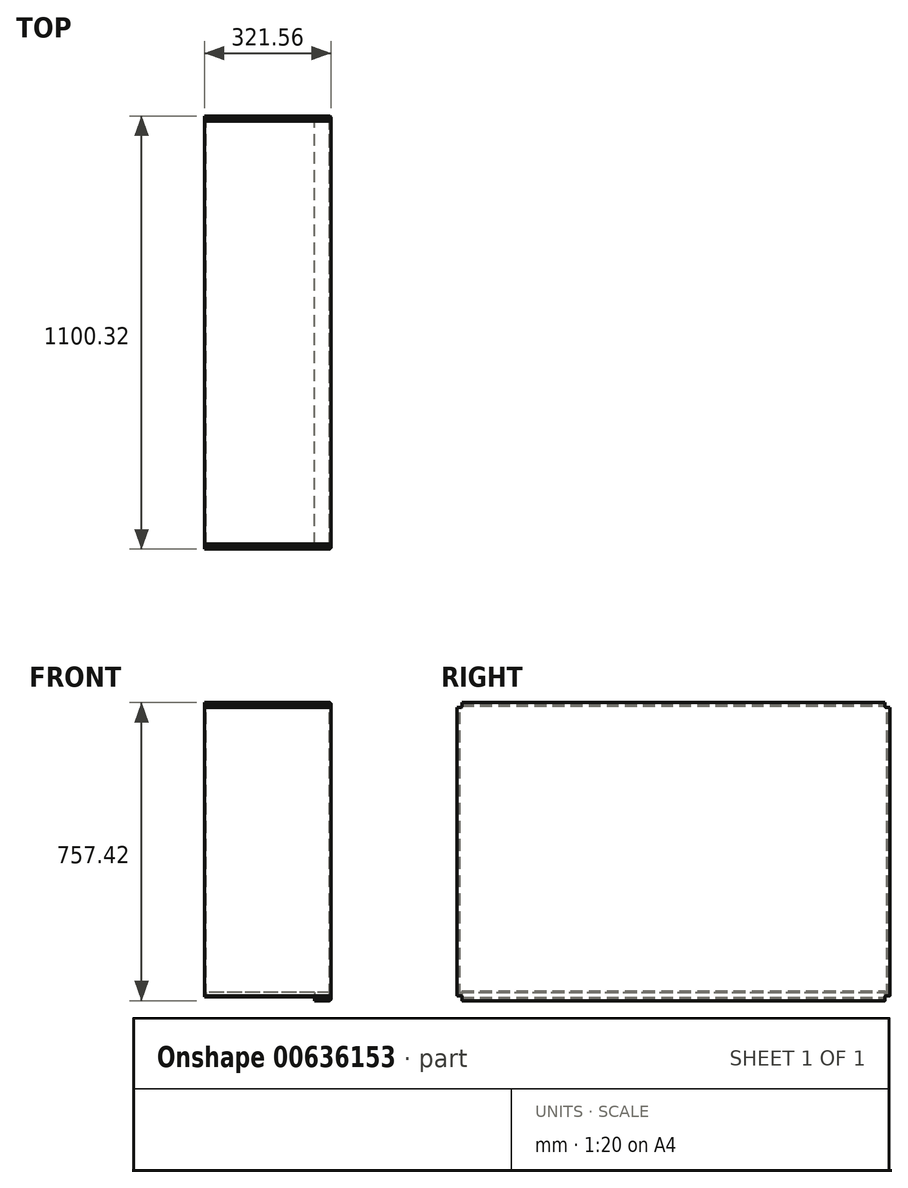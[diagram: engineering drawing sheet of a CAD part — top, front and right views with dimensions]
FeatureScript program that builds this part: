
annotation { "Feature Type Name" : "Feature", "Feature Type Description" : "" }
export const myFeature = defineFeature(function(context is Context, id is Id, definition is map)
    precondition{}
    {
        {
            var Q0;
            Q0=qCreatedBy(makeId("Right.planeOp"),FACE);
            var sketch = newSketch(context, id + "F0", { "sketchPlane" : qUnion([Q0])});
            skLineSegment(sketch, "E0.bottom", {"start": v(0, 0) * mm, "end": v(1092.2, 0) * mm});
            skLineSegment(sketch, "E0.top", {"start": v(0, 749.3) * mm, "end": v(1092.2, 749.3) * mm});
            skLineSegment(sketch, "E0.left", {"start": v(0, 0) * mm, "end": v(0, 749.3) * mm});
            skLineSegment(sketch, "E0.right", {"start": v(1092.2, 0) * mm, "end": v(1092.2, 749.3) * mm});
            skSolve(sketch);
        }
        {
            var Q0;
            Q0 = qSketchRegion(id + "F0", true);
            extrude(context, id + "F1", {"entities" : qUnion([Q0]), "depth" : 317.5 * mm, "offsetDistance" : 25.4 * mm});
        }
        {
            var Q0;
            Q0=makeQuery(id+"F1.opExtrude","CAP_FACE",FACE,{"disambiguationData":[OSD([sQuery(id+"F0.wireOp",EDGE,"E0.bottom"),sQuery(id+"F0.wireOp",EDGE,"E0.top"),sQuery(id+"F0.wireOp",EDGE,"E0.left"),sQuery(id+"F0.wireOp",EDGE,"E0.right")])],"isStart":false});
            shell(context, id + "F2", {"entities" : qUnion([Q0]), "thickness" : 4.06 * mm});
        }
        {
            var Q0;
            Q0=makeQuery(id+"F1.opExtrude","SWEPT_FACE",FACE,{"disambiguationData":[OSD([sQuery(id+"F0.wireOp",EDGE,"E0.bottom")])]});
            var sketch = newSketch(context, id + "F3", { "sketchPlane" : qUnion([Q0])});
            skLineSegment(sketch, "E1.bottom", {"start": v(317.5, 0) * mm, "end": v(38.1, 0) * mm});
            skLineSegment(sketch, "E1.top", {"start": v(317.5, -1717.8) * mm, "end": v(38.1, -1717.8) * mm});
            skLineSegment(sketch, "E1.left", {"start": v(317.5, 0) * mm, "end": v(317.5, -1717.8) * mm});
            skLineSegment(sketch, "E1.right", {"start": v(38.1, 0) * mm, "end": v(38.1, -1717.8) * mm});
            skSolve(sketch);
        }
        {
            var Q0;
            Q0 = qSketchRegion(id + "F3", true);
            extrude(context, id + "F4", {"entities" : qUnion([Q0]), "operationType" : NewBodyOperationType.REMOVE, "oppositeDirection" : true, "depth" : 4.06 * mm, "offsetDistance" : 25.4 * mm});
        }
        {
            var Q0;
            Q0=makeQuery(id+"F1.opExtrude","CAP_FACE",FACE,{"disambiguationData":[OSD([sQuery(id+"F0.wireOp",EDGE,"E0.bottom"),sQuery(id+"F0.wireOp",EDGE,"E0.top"),sQuery(id+"F0.wireOp",EDGE,"E0.left"),sQuery(id+"F0.wireOp",EDGE,"E0.right")])],"isStart":true});
            var sketch = newSketch(context, id + "F5", { "sketchPlane" : qUnion([Q0])});
            skLineSegment(sketch, "E2.bottom", {"start": v(-1092.2, 0) * mm, "end": v(-1085.85, 0) * mm});
            skLineSegment(sketch, "E2.top", {"start": v(-1092.2, 6.35) * mm, "end": v(-1088.39, 6.35) * mm});
            skLineSegment(sketch, "E2.left", {"start": v(-1092.2, 0) * mm, "end": v(-1092.2, 6.35) * mm});
            skLineSegment(sketch, "E2.right", {"start": v(-1085.85, 0) * mm, "end": v(-1085.85, 3.81) * mm});
            skLineSegment(sketch, "E3.bottom", {"start": v(-1092.2, 749.3) * mm, "end": v(-1085.85, 749.3) * mm});
            skLineSegment(sketch, "E3.top", {"start": v(-1092.2, 742.95) * mm, "end": v(-1088.4, 742.95) * mm});
            skLineSegment(sketch, "E3.left", {"start": v(-1092.2, 749.3) * mm, "end": v(-1092.2, 742.95) * mm});
            skLineSegment(sketch, "E3.right", {"start": v(-1085.85, 749.3) * mm, "end": v(-1085.85, 745.5) * mm});
            skLineSegment(sketch, "E4.bottom", {"start": v(0, 749.3) * mm, "end": v(-6.35, 749.3) * mm});
            skLineSegment(sketch, "E4.top", {"start": v(0, 742.95) * mm, "end": v(-3.8, 742.95) * mm});
            skLineSegment(sketch, "E4.left", {"start": v(0, 749.3) * mm, "end": v(0, 742.95) * mm});
            skLineSegment(sketch, "E4.right", {"start": v(-6.35, 749.3) * mm, "end": v(-6.35, 745.5) * mm});
            skLineSegment(sketch, "E5.bottom", {"start": v(0, 0) * mm, "end": v(-6.35, 0) * mm});
            skLineSegment(sketch, "E5.top", {"start": v(0, 6.35) * mm, "end": v(-3.8, 6.35) * mm});
            skLineSegment(sketch, "E5.left", {"start": v(0, 0) * mm, "end": v(0, 6.35) * mm});
            skLineSegment(sketch, "E5.right", {"start": v(-6.35, 0) * mm, "end": v(-6.35, 3.81) * mm});
            skPoint(sketch, "E6.visualSharp", {"position": v(-1085.85, 742.95) * mm});
            skArc(sketch, "E6.filletArc", {"start": v(-1088.4, 742.95) * mm, "mid": v(-1086.6, 743.7) * mm, "end": v(-1085.85, 745.5) * mm});
            skPoint(sketch, "E7.visualSharp", {"position": v(-6.35, 742.95) * mm});
            skArc(sketch, "E7.filletArc", {"start": v(-6.35, 745.5) * mm, "mid": v(-5.6, 743.7) * mm, "end": v(-3.8, 742.95) * mm});
            skPoint(sketch, "E8.visualSharp", {"position": v(-6.35, 6.35) * mm});
            skArc(sketch, "E8.filletArc", {"start": v(-3.8, 6.35) * mm, "mid": v(-5.6, 5.6) * mm, "end": v(-6.35, 3.81) * mm});
            skPoint(sketch, "E9.visualSharp", {"position": v(-1085.85, 6.35) * mm});
            skArc(sketch, "E9.filletArc", {"start": v(-1085.85, 3.81) * mm, "mid": v(-1086.6, 5.6) * mm, "end": v(-1088.39, 6.35) * mm});
            skSolve(sketch);
        }
        {
            var Q0;
            Q0 = qSketchRegion(id + "F5", true);
            extrude(context, id + "F6", {"entities" : qUnion([Q0]), "operationType" : NewBodyOperationType.REMOVE, "endBound" : BoundingType.THROUGH_ALL, "oppositeDirection" : true, "depth" : 25.4 * mm, "offsetDistance" : 25.4 * mm});
        }
        {
            var Q0;
            Q0=makeQuery(id+"F1.opExtrude","CAP_EDGE",EDGE,{"disambiguationData":[OSD([sQuery(id+"F0.wireOp",EDGE,"E0.right")])],"isStart":true});
            var Q1;
            Q1=makeQuery(id+"F1.opExtrude","CAP_EDGE",EDGE,{"disambiguationData":[OSD([sQuery(id+"F0.wireOp",EDGE,"E0.bottom")])],"isStart":true});
            var Q2;
            Q2=makeQuery(id+"F1.opExtrude","CAP_EDGE",EDGE,{"disambiguationData":[OSD([sQuery(id+"F0.wireOp",EDGE,"E0.left")])],"isStart":true});
            var Q3;
            Q3=makeQuery(id+"F1.opExtrude","CAP_EDGE",EDGE,{"disambiguationData":[OSD([sQuery(id+"F0.wireOp",EDGE,"E0.top")])],"isStart":true});
            fillet(context, id + "F7", {"entities" : qUnion([Q0, Q1, Q2, Q3]), "radius" : 2.54 * mm, "tangentPropagation" : true, "allowEdgeOverflow" : false});
        }
        {
            var Q0;
            Q0=makeQuery(id+"F2.opShell","OFFSET_FACE",FACE,{"disambiguationData":[OSD([sQuery(id+"F0.wireOp",EDGE,"E0.bottom"),sQuery(id+"F0.wireOp",EDGE,"E0.top"),sQuery(id+"F0.wireOp",EDGE,"E0.left"),sQuery(id+"F0.wireOp",EDGE,"E0.right")])]});
            var sketch = newSketch(context, id + "F8", { "sketchPlane" : qUnion([Q0])});
            skLineSegment(sketch, "E10.bottom", {"start": v(4.06, 16.76) * mm, "end": v(1088.14, 16.76) * mm});
            skLineSegment(sketch, "E10.top", {"start": v(4.06, 4.06) * mm, "end": v(1088.14, 4.06) * mm});
            skLineSegment(sketch, "E10.left", {"start": v(4.06, 16.76) * mm, "end": v(4.06, 4.06) * mm});
            skLineSegment(sketch, "E10.right", {"start": v(1088.14, 16.76) * mm, "end": v(1088.14, 4.06) * mm});
            skSolve(sketch);
        }
        {
            var Q0;
            Q0 = qSketchRegion(id + "F8", true);
            var Q1;
            {var subQ0=sQuery(id+"F0.wireOp",EDGE,"E0.left");Q1=makeQuery(id+"F6.boolean.opBoolean","SPLIT",FACE,{"disambiguationData":[TD([makeQuery(id+"F1.opExtrude","SWEPT_FACE",FACE,{"disambiguationData":[OSD([subQ0])]})])],"derivedFrom":makeQuery(id+"F1.opExtrude","CAP_FACE",FACE,{"disambiguationData":[OSD([sQuery(id+"F0.wireOp",EDGE,"E0.bottom"),sQuery(id+"F0.wireOp",EDGE,"E0.top"),subQ0,sQuery(id+"F0.wireOp",EDGE,"E0.right")])],"isStart":false})});}
            extrude(context, id + "F9", {"entities" : qUnion([Q0]), "endBound" : BoundingType.UP_TO_SURFACE, "depth" : 330.2 * mm, "endBoundEntityFace" : qUnion([Q1]), "offsetDistance" : 25.4 * mm});
        }
        {
            var Q0;
            Q0 = qSketchRegion(id + "F0", true);
            extrude(context, id + "F10", {"entities" : qUnion([Q0]), "depth" : 317.5 * mm, "offsetDistance" : 25.4 * mm});
        }
        {
            var Q0;
            Q0=makeQuery(id+"F10.opExtrude","CAP_FACE",FACE,{"disambiguationData":[OSD([sQuery(id+"F0.wireOp",EDGE,"E0.bottom"),sQuery(id+"F0.wireOp",EDGE,"E0.top"),sQuery(id+"F0.wireOp",EDGE,"E0.left"),sQuery(id+"F0.wireOp",EDGE,"E0.right")])],"isStart":true});
            shell(context, id + "F11", {"entities" : qUnion([Q0]), "thickness" : 4.06 * mm, "oppositeDirection" : true});
        }
        {
            var Q0;
            Q0=makeQuery(id+"F10.opExtrude","CAP_FACE",FACE,{"disambiguationData":[OSD([sQuery(id+"F0.wireOp",EDGE,"E0.bottom"),sQuery(id+"F0.wireOp",EDGE,"E0.top"),sQuery(id+"F0.wireOp",EDGE,"E0.left"),sQuery(id+"F0.wireOp",EDGE,"E0.right")])],"isStart":false});
            var sketch = newSketch(context, id + "F12", { "sketchPlane" : qUnion([Q0])});
            skLineSegment(sketch, "E11.bottom", {"start": v(1096.26, -4.06) * mm, "end": v(1083.56, -4.06) * mm});
            skLineSegment(sketch, "E11.top", {"start": v(1096.26, 8.64) * mm, "end": v(1086.1, 8.64) * mm});
            skLineSegment(sketch, "E11.left", {"start": v(1096.26, -4.06) * mm, "end": v(1096.26, 8.64) * mm});
            skLineSegment(sketch, "E11.right", {"start": v(1083.56, -4.06) * mm, "end": v(1083.56, 6.1) * mm});
            skLineSegment(sketch, "E12.bottom", {"start": v(-4.06, 753.36) * mm, "end": v(8.64, 753.36) * mm});
            skLineSegment(sketch, "E12.top", {"start": v(-4.06, 740.66) * mm, "end": v(6.1, 740.66) * mm});
            skLineSegment(sketch, "E12.left", {"start": v(-4.06, 753.36) * mm, "end": v(-4.06, 740.66) * mm});
            skLineSegment(sketch, "E12.right", {"start": v(8.64, 753.36) * mm, "end": v(8.64, 743.2) * mm});
            skLineSegment(sketch, "E13.bottom", {"start": v(1096.26, 753.36) * mm, "end": v(1083.56, 753.36) * mm});
            skLineSegment(sketch, "E13.top", {"start": v(1096.26, 740.66) * mm, "end": v(1086.1, 740.66) * mm});
            skLineSegment(sketch, "E13.left", {"start": v(1096.26, 753.36) * mm, "end": v(1096.26, 740.66) * mm});
            skLineSegment(sketch, "E13.right", {"start": v(1083.56, 753.36) * mm, "end": v(1083.56, 743.2) * mm});
            skPoint(sketch, "E14.visualSharp", {"position": v(8.64, 740.66) * mm});
            skArc(sketch, "E14.filletArc", {"start": v(6.1, 740.66) * mm, "mid": v(7.9, 741.4) * mm, "end": v(8.64, 743.2) * mm});
            skPoint(sketch, "E15.visualSharp", {"position": v(1083.56, 740.66) * mm});
            skArc(sketch, "E15.filletArc", {"start": v(1083.56, 743.2) * mm, "mid": v(1084.3, 741.4) * mm, "end": v(1086.1, 740.66) * mm});
            skPoint(sketch, "E16.visualSharp", {"position": v(1083.56, 8.64) * mm});
            skArc(sketch, "E16.filletArc", {"start": v(1086.1, 8.64) * mm, "mid": v(1084.3, 7.9) * mm, "end": v(1083.56, 6.1) * mm});
            skLineSegment(sketch, "E17.bottom", {"start": v(-4.06, -4.06) * mm, "end": v(8.64, -4.06) * mm});
            skLineSegment(sketch, "E17.top", {"start": v(-4.06, 8.64) * mm, "end": v(6.1, 8.64) * mm});
            skLineSegment(sketch, "E17.left", {"start": v(-4.06, -4.06) * mm, "end": v(-4.06, 8.64) * mm});
            skLineSegment(sketch, "E17.right", {"start": v(8.64, -4.06) * mm, "end": v(8.64, 6.1) * mm});
            skPoint(sketch, "E18.visualSharp", {"position": v(8.64, 8.64) * mm});
            skArc(sketch, "E18.filletArc", {"start": v(8.64, 6.1) * mm, "mid": v(7.9, 7.9) * mm, "end": v(6.1, 8.64) * mm});
            skSolve(sketch);
        }
        {
            var Q0;
            Q0 = qSketchRegion(id + "F12", true);
            extrude(context, id + "F13", {"entities" : qUnion([Q0]), "operationType" : NewBodyOperationType.REMOVE, "endBound" : BoundingType.THROUGH_ALL, "oppositeDirection" : true, "depth" : 25.4 * mm, "offsetDistance" : 25.4 * mm});
        }
        {
            var Q0;
            Q0=makeQuery(id+"F10.opExtrude","CAP_EDGE",EDGE,{"disambiguationData":[OSD([sQuery(id+"F0.wireOp",EDGE,"E0.right")])],"isStart":false});
            var Q1;
            Q1=makeQuery(id+"F10.opExtrude","CAP_EDGE",EDGE,{"disambiguationData":[OSD([sQuery(id+"F0.wireOp",EDGE,"E0.top")])],"isStart":false});
            var Q2;
            Q2=makeQuery(id+"F10.opExtrude","CAP_EDGE",EDGE,{"disambiguationData":[OSD([sQuery(id+"F0.wireOp",EDGE,"E0.left")])],"isStart":false});
            var Q3;
            Q3=makeQuery(id+"F10.opExtrude","CAP_EDGE",EDGE,{"disambiguationData":[OSD([sQuery(id+"F0.wireOp",EDGE,"E0.bottom")])],"isStart":false});
            fillet(context, id + "F14", {"entities" : qUnion([Q0, Q1, Q2, Q3]), "radius" : 5.08 * mm, "tangentPropagation" : true, "allowEdgeOverflow" : false});
        }
        {
            var Q0;
            Q0=makeQuery(id+"F10.opExtrude","SWEPT_FACE",FACE,{"disambiguationData":[OSD([sQuery(id+"F0.wireOp",EDGE,"E0.bottom")])]});
            var sketch = newSketch(context, id + "F15", { "sketchPlane" : qUnion([Q0])});
            skLineSegment(sketch, "E19.bottom", {"start": v(0, -1083.56) * mm, "end": v(279.4, -1083.56) * mm});
            skLineSegment(sketch, "E19.top", {"start": v(0, -8.64) * mm, "end": v(279.4, -8.64) * mm});
            skLineSegment(sketch, "E19.left", {"start": v(0, -1083.56) * mm, "end": v(0, -8.64) * mm});
            skLineSegment(sketch, "E19.right", {"start": v(279.4, -1083.56) * mm, "end": v(279.4, -8.64) * mm});
            skSolve(sketch);
        }
        {
            var Q0;
            Q0 = qSketchRegion(id + "F15", true);
            extrude(context, id + "F16", {"entities" : qUnion([Q0]), "operationType" : NewBodyOperationType.REMOVE, "oppositeDirection" : true, "depth" : 25.4 * mm, "offsetDistance" : 25.4 * mm});
        }
        {
            var Q0;
            Q0=makeQuery(id+"F9.opExtrude","SWEPT_EDGE",EDGE,{"disambiguationData":[OSD([sQuery(id+"F0.wireOp",EDGE,"E0.left"),sQuery(id+"F8.wireOp",EDGE,"E10.bottom"),sQuery(id+"F8.wireOp",EDGE,"E10.left")])]});
            cPoint(context, id + "F17", {"entities" : qUnion([Q0]), "parameter" : 0.5});
        }
        {
            var Q0;
            Q0=qCreatedBy(makeId("Right.planeOp"),FACE);
            var Q1;
            Q1 = qCreatedBy(id + "F17" ,VERTEX);
            cPlane(context, id + "F18", {"entities" : qUnion([Q0, Q1]), "cplaneType" : CPlaneType.PLANE_POINT, "offset" : 25.4 * mm, "width" : 152.4 * mm, "height" : 152.4 * mm});
        }
    });
